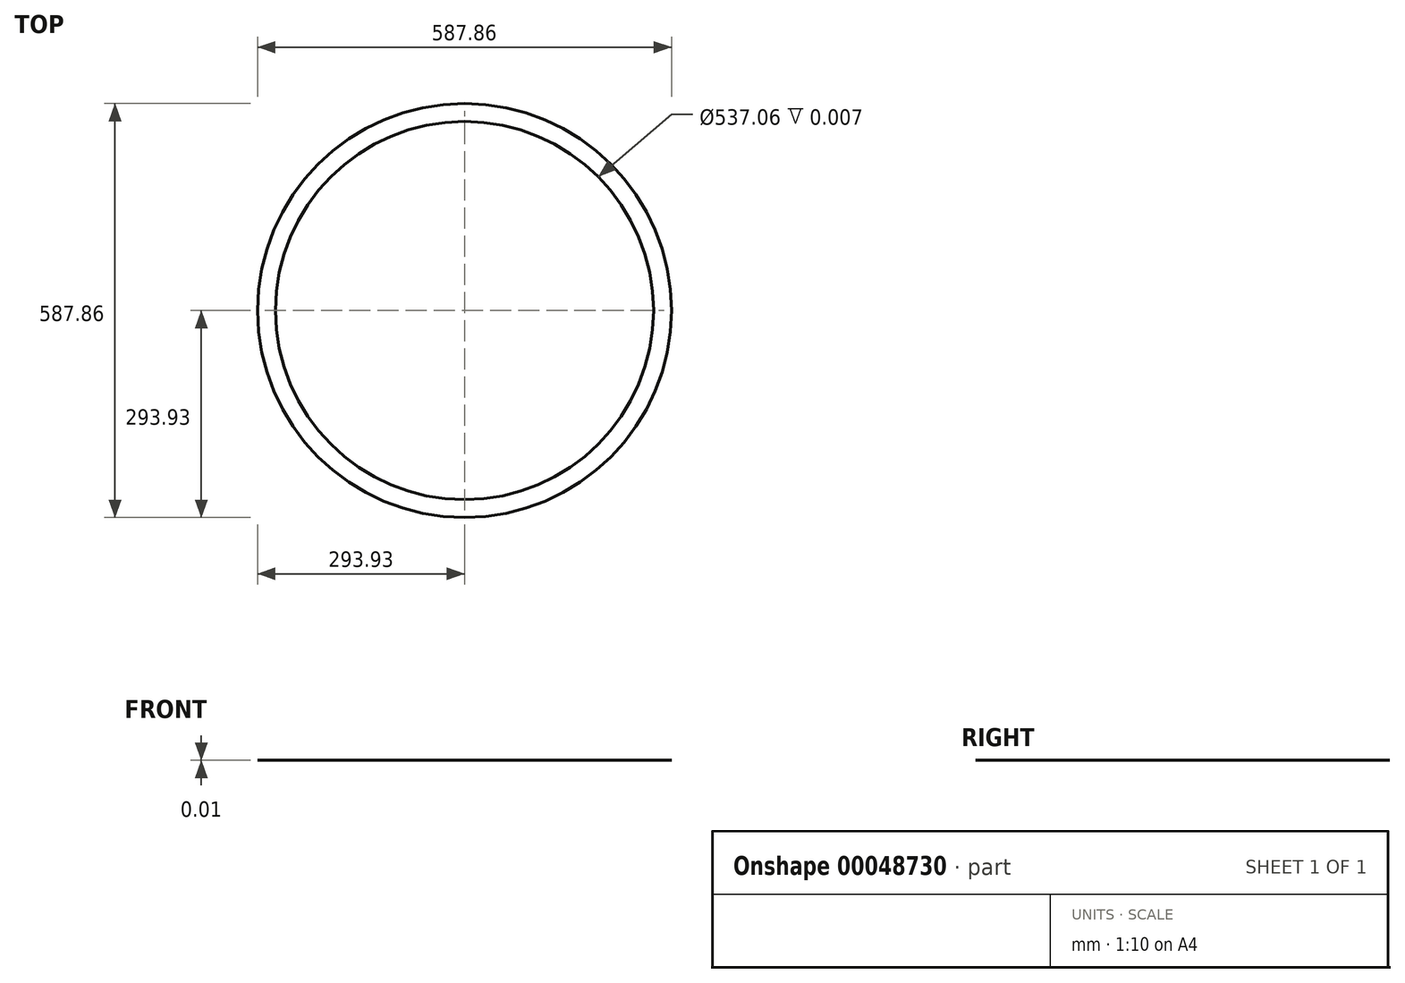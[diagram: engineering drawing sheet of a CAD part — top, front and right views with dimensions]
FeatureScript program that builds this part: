
annotation { "Feature Type Name" : "Feature", "Feature Type Description" : "" }
export const myFeature = defineFeature(function(context is Context, id is Id, definition is map)
    precondition{}
    {
        {
            var Q0;
            Q0=qCreatedBy(makeId("Top.planeOp"),FACE);
            var sketch = newSketch(context, id + "F0", { "sketchPlane" : qUnion([Q0])});
            skCircle(sketch, "E0", {"center": v(0, 0) * mm, "radius": 293.93 * mm});
            skCircle(sketch, "E1", {"center": v(0, 0) * mm, "radius": 268.53 * mm});
            skSolve(sketch);
        }
        {
            var Q0;
            Q0=makeQuery(id+"F0.imprint","IMPRINT",FACE,{"disambiguationData":[TD([[makeQuery(id+"F0.imprint","IMPRINT",EDGE,{"derivedFrom":sQuery(id+"F0.wireOp",EDGE,"E0")}),1.0]])]});
            extrude(context, id + "F1", {"entities" : qUnion([Q0]), "depth" : 3 / 406.4 * mm});
        }
    });
